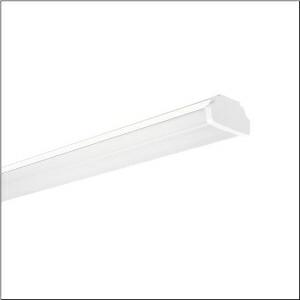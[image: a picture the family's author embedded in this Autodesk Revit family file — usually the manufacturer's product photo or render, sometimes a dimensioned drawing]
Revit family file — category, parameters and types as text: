
# Revit family: modario_31_gen_2_53bm812cv475c2_71b4
name_source: partatom
category: Lighting Fixtures
units: mm (PartAtom-declared; Revit-internal decimal feet)

## family parameters
Cut with Voids When Loaded = No
Host = Face
Light Source = No
Part Type = Normal
Room Calculation Point = No
Round Connector Dimension = Use Diameter
Shared = No

## types (1)
- --- (1 x LED, 7600 lm, 40.5 W, 4000K)
    Apparent Load = 41 VA
    CIE Flux Codes = 47 80 95 93 100
    Color Rendering = 80
    Color Temperature = 4000K
    Default Elevation = 1800 mm
    Description = Modario 31 Gen.2, luminaire insert, of sheet steel, coil coated, white, length: 1.495mm, width: 81mm, height: 82mm, 5x system unit, system units: 299mm, LED rated luminous flux: 7.600lm, light colour: 840, SDCM (Standard Deviation of Colour Matching)MacAdam ≤ 3 SDCM (initial), control gear: ON/OFF Multilumen, CLOi, with plug, 3-pole, with phase selection, mains connection: 220..240V, AC, 50/60Hz, start of lifetime: 41W, end of service life: 48W, through-wiring accessed according to module size, primary optical cover: cover, of PMMA, light emission: direct distribution, primary light characteristic: symmetric, protection rating (complete): IP20, protection rating (LED compartment): IP50, insulation class (complete): insulation class I (protective earthing), certification: CE, ENEC, VDE, UKCA, impact resistance: IK03, permissible ambient temperature for indoor applications: -35..+50°C, corresponds to IFS (International Featured Standards) requirements for safety and quality in the food industry, reducing of maximum allowable ambient temperature of 5°C with ceiling mounting, IP40 when using the optional accessory 5TP9018, packaging unit: 1 piece
    Height = 92 mm
    Lamp = 1 x LED
    Lamp Light Flux = 7600 lm
    Lamp Power = 40.5 W
    Lamp count = 1
    Length = 1495 mm
    Luminous efficacy = 188 lm/W
    Manufacturer = Siteco
    ModVariant = No
    Model = 53BM812CV475C2
    Mounting Place = Ceiling
    Mounting Type = Pendant
    Number of Poles = 1
    OnlyDefault = Yes
    Power Factor = 1
    Product Name = Modario 31 Gen.2
    Product group = luminaire insert | ceiling pendant
    ProductGroupID = 901
    Protection Class = Protection class I
    Protection Degree = IP 20
    RLX_Detail_Level = 1
    RLX_Emergency_Light_Flux = 0 lm
    RLX_Emergency_Type = 0
    RLX_Emergency_Type_DB = No
    RlxData = <blob elided: 40101 chars, md5=1f16ab32>
    Socket = socket
    Standby Power = 0 W
    System Light Flux = 7600 lm
    System Power = 41 W
    Type Comments = factory setting: luminous flux: 100 % | (A | C | E) | 94 mA
    Type Image = l_1341886.jpg
    URL = http://relux.com
    VarID = @adj_040739
    Voltage = 0 V
    Weight = 0.00 kg
    Width = 81 mm

## geometry (parser evidence)
native form markers: Blend x4, Sweep x12
no freeform markers — native parametric forms only
